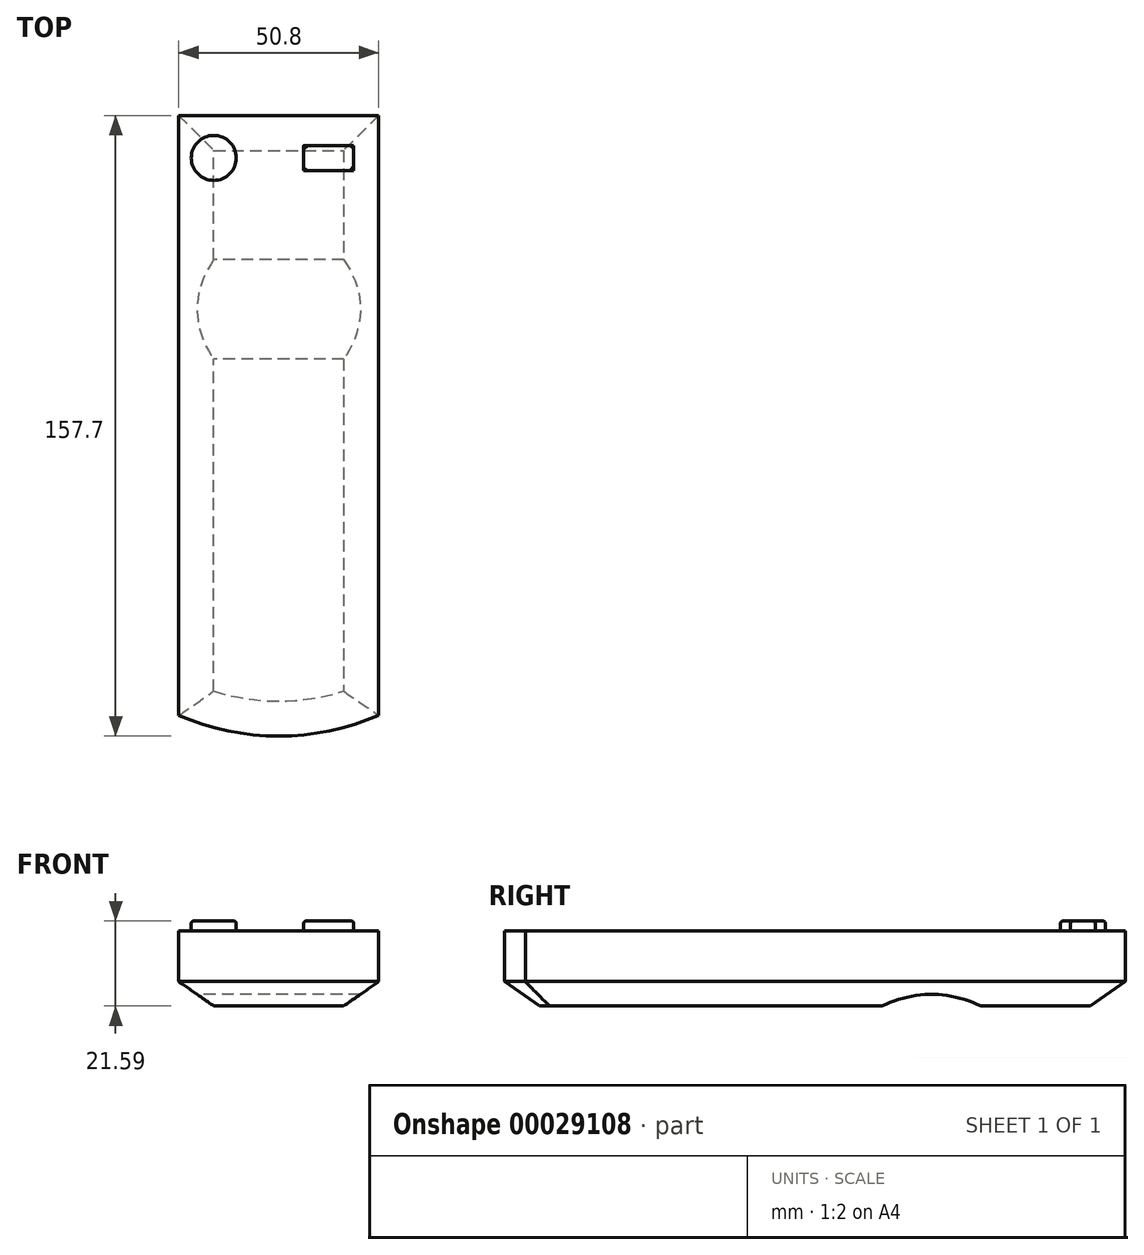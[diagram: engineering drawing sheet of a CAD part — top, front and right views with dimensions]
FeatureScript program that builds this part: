
annotation { "Feature Type Name" : "Feature", "Feature Type Description" : "" }
export const myFeature = defineFeature(function(context is Context, id is Id, definition is map)
    precondition{}
    {
        {
            var Q0;
            Q0=qCreatedBy(makeId("Top.planeOp"),FACE);
            var sketch = newSketch(context, id + "F0", { "sketchPlane" : qUnion([Q0])});
            skLineSegment(sketch, "E0.bottom", {"start": v(-25.4, 76.2) * mm, "end": v(25.4, 76.2) * mm});
            skLineSegment(sketch, "E0.left", {"start": v(-25.4, 76.2) * mm, "end": v(-25.4, -76.2) * mm});
            skLineSegment(sketch, "E0.right", {"start": v(25.4, 76.2) * mm, "end": v(25.4, -76.2) * mm});
            skArc(sketch, "E1", {"start": v(-25.4, -76.2) * mm, "mid": v(0, -81.5) * mm, "end": v(25.4, -76.2) * mm});
            skSolve(sketch);
        }
        {
            var Q0;
            Q0 = qSketchRegion(id + "F0", true);
            extrude(context, id + "F1", {"entities" : qUnion([Q0]), "depth" : 19.05 * mm});
        }
        {
            var Q0;
            Q0=makeQuery(id+"F1.opExtrude","CAP_EDGE",EDGE,{"disambiguationData":[OSD([sQuery(id+"F0.wireOp",EDGE,"E0.bottom")])],"isStart":true});
            var Q1;
            Q1=makeQuery(id+"F1.opExtrude","CAP_EDGE",EDGE,{"disambiguationData":[OSD([sQuery(id+"F0.wireOp",EDGE,"E1")])],"isStart":true});
            chamfer(context, id + "F2", {"entities" : qUnion([Q0, Q1]), "chamferType" : ChamferType.OFFSET_ANGLE, "width" : 8.9 * mm, "oppositeDirection" : false, "angle" : 35 * degree, "tangentPropagation" : true});
        }
        {
            var Q0;
            Q0=makeQuery(id+"F1.opExtrude","CAP_EDGE",EDGE,{"disambiguationData":[OSD([sQuery(id+"F0.wireOp",EDGE,"E0.right")])],"isStart":true});
            var Q1;
            Q1=makeQuery(id+"F1.opExtrude","CAP_EDGE",EDGE,{"disambiguationData":[OSD([sQuery(id+"F0.wireOp",EDGE,"E0.left")])],"isStart":true});
            chamfer(context, id + "F3", {"entities" : qUnion([Q0, Q1]), "chamferType" : ChamferType.OFFSET_ANGLE, "width" : 8.9 * mm, "oppositeDirection" : false, "angle" : 35 * degree, "tangentPropagation" : true});
        }
        {
            var Q0;
            Q0=makeQuery(id+"F1.opExtrude","CAP_FACE",FACE,{"disambiguationData":[OSD([sQuery(id+"F0.wireOp",EDGE,"E0.bottom"),sQuery(id+"F0.wireOp",EDGE,"E0.left"),sQuery(id+"F0.wireOp",EDGE,"E0.right"),sQuery(id+"F0.wireOp",EDGE,"E1")])],"isStart":false});
            var sketch = newSketch(context, id + "F4", { "sketchPlane" : qUnion([Q0])});
            skLineSegment(sketch, "E2.bottom", {"start": v(6.35, 68.58) * mm, "end": v(19.05, 68.58) * mm});
            skLineSegment(sketch, "E2.top", {"start": v(6.35, 62.23) * mm, "end": v(19.05, 62.23) * mm});
            skLineSegment(sketch, "E2.left", {"start": v(6.35, 68.58) * mm, "end": v(6.35, 62.23) * mm});
            skLineSegment(sketch, "E2.right", {"start": v(19.05, 68.58) * mm, "end": v(19.05, 62.23) * mm});
            skCircle(sketch, "E3", {"center": v(-16.51, 65.4) * mm, "radius": 5.72 * mm});
            skPoint(sketch, "E4", {"position": v(6.35, 65.4) * mm});
            skSolve(sketch);
        }
        {
            var Q0;
            Q0 = qSketchRegion(id + "F4", true);
            extrude(context, id + "F5", {"entities" : qUnion([Q0]), "operationType" : NewBodyOperationType.ADD, "depth" : 2.54 * mm});
        }
        {
            var Q0;
            Q0=makeQuery(id+"F5.opExtrude","CAP_EDGE",EDGE,{"disambiguationData":[OSD([sQuery(id+"F4.wireOp",EDGE,"E3")])],"isStart":false});
            var Q1;
            Q1=makeQuery(id+"F5.opExtrude","CAP_FACE",FACE,{"disambiguationData":[OSD([sQuery(id+"F4.wireOp",EDGE,"E2.bottom"),sQuery(id+"F4.wireOp",EDGE,"E2.top"),sQuery(id+"F4.wireOp",EDGE,"E2.left"),sQuery(id+"F4.wireOp",EDGE,"E2.right")])],"isStart":false});
            fillet(context, id + "F6", {"entities" : qUnion([Q0, Q1]), "radius" : 0.64 * mm, "tangentPropagation" : true, "allowEdgeOverflow" : false});
        }
        {
            var Q0;
            Q0=makeQuery(id+"F1.opExtrude","SWEPT_FACE",FACE,{"disambiguationData":[OSD([sQuery(id+"F0.wireOp",EDGE,"E0.left")])]});
            var sketch = newSketch(context, id + "F7", { "sketchPlane" : qUnion([Q0])});
            skCircle(sketch, "E5", {"center": v(-26.93, -25.16) * mm, "radius": 28.13 * mm});
            skSolve(sketch);
        }
        {
            var Q0;
            Q0=makeQuery(id+"F7.imprint","IMPRINT",FACE,{"disambiguationData":[TD([[makeQuery(id+"F7.imprint","IMPRINT",EDGE,{"derivedFrom":sQuery(id+"F7.wireOp",EDGE,"E5")}),1.0]])]});
            extrude(context, id + "F8", {"entities" : qUnion([Q0]), "operationType" : NewBodyOperationType.REMOVE, "oppositeDirection" : true, "depth" : 76.06 * mm});
        }
        {
            var Q0;
            {var subQ0=sQuery(id+"F0.wireOp",EDGE,"E0.left");var subQ1=sQuery(id+"F0.wireOp",EDGE,"E0.right");var subQ2=sQuery(id+"F0.wireOp",EDGE,"E1");Q0=makeQuery(id+"F8.boolean.opBoolean","SPLIT",FACE,{"disambiguationData":[TD([makeQuery(id+"F2.opChamfer","BLEND_FACE",FACE,{"disambiguationData":[OSD([subQ2])]})])],"derivedFrom":makeQuery(id+"F1.opExtrude","CAP_FACE",FACE,{"disambiguationData":[OSD([sQuery(id+"F0.wireOp",EDGE,"E0.bottom"),subQ0,subQ1,subQ2])],"isStart":true})});}
            var sketch = newSketch(context, id + "F9", { "sketchPlane" : qUnion([Q0])});
            skCircle(sketch, "E6", {"center": v(-10.7, 65.34) * mm, "radius": 2.82 * mm});
            skSolve(sketch);
        }
        {
            var Q0;
            Q0=sQuery(id+"F9.wireOp",EDGE,"E6");
            extrude(context, id + "F10", {"bodyType" : ToolBodyType.SURFACE, "surfaceEntities" : qUnion([Q0]), "depth" : 25.4 * mm});
        }
    });
